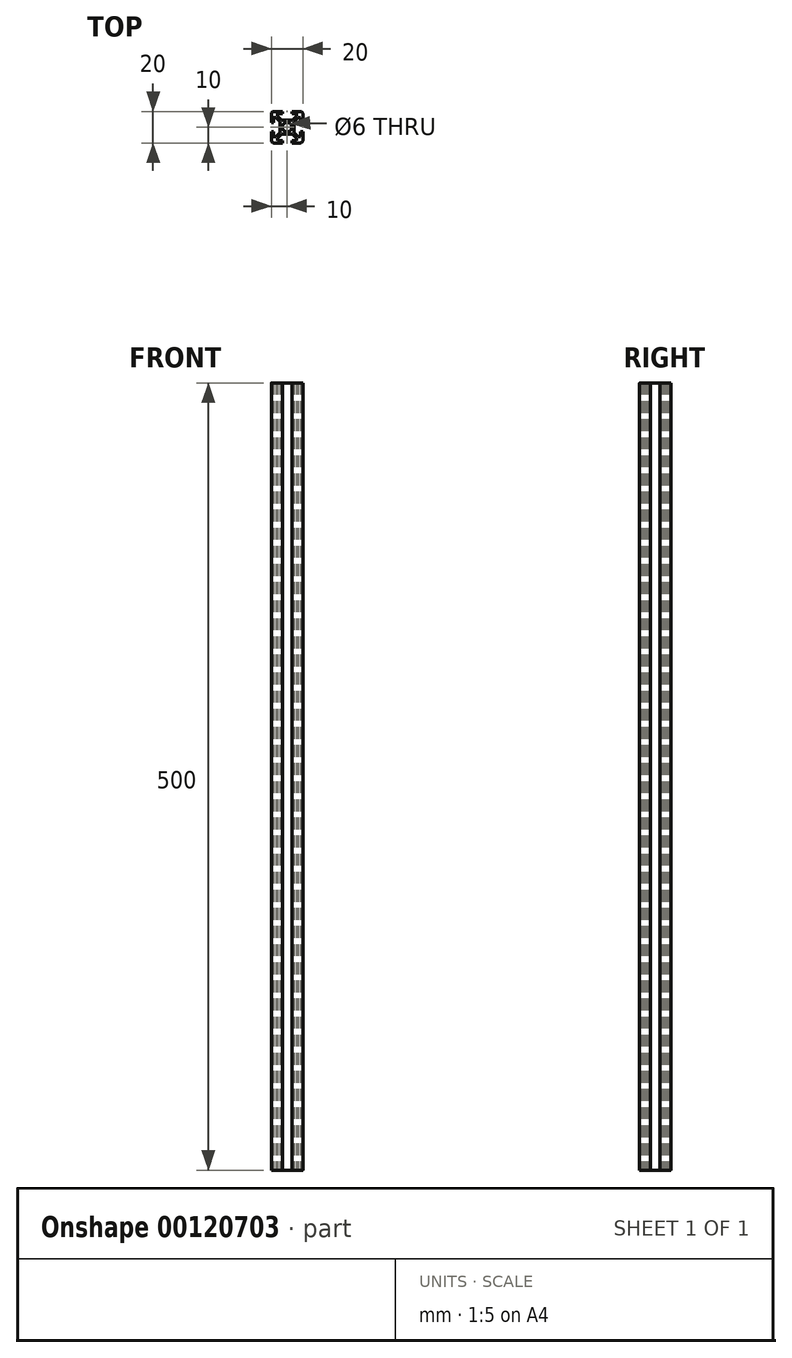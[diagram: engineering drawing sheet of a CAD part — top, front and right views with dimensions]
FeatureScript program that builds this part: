
annotation { "Feature Type Name" : "Feature", "Feature Type Description" : "" }
export const myFeature = defineFeature(function(context is Context, id is Id, definition is map)
    precondition{}
    {
        {
            var Q0;
            Q0=qCreatedBy(makeId("Top.planeOp"),FACE);
            var sketch = newSketch(context, id + "F0", { "sketchPlane" : qUnion([Q0])});
            skLineSegment(sketch, "E0.bottom", {"start": v(1.5, 0) * mm, "end": v(7, 0) * mm});
            skLineSegment(sketch, "E0.top", {"start": v(1.5, 20) * mm, "end": v(7, 20) * mm});
            skLineSegment(sketch, "E0.left", {"start": v(0, 1.5) * mm, "end": v(0, 7) * mm});
            skLineSegment(sketch, "E0.right", {"start": v(20, 1.5) * mm, "end": v(20, 7) * mm});
            skLineSegment(sketch, "E1", {"start": v(10, 25.59) * mm, "end": v(10, -6.26) * mm, "construction": true});
            skPoint(sketch, "E1.startSnap0", {"position": v(10, 20) * mm});
            skLineSegment(sketch, "E2", {"start": v(-5.38, 10) * mm, "end": v(26.16, 10) * mm, "construction": true});
            skPoint(sketch, "E2.startSnap0", {"position": v(0, 10) * mm});
            skPoint(sketch, "E3.visualSharp", {"position": v(20, 20) * mm});
            skArc(sketch, "E3.filletArc", {"start": v(20, 18.5) * mm, "mid": v(19.56, 19.56) * mm, "end": v(18.5, 20) * mm});
            skPoint(sketch, "E4.visualSharp", {"position": v(20, 0) * mm});
            skArc(sketch, "E4.filletArc", {"start": v(18.5, 0) * mm, "mid": v(19.56, 0.44) * mm, "end": v(20, 1.5) * mm});
            skPoint(sketch, "E5.visualSharp", {"position": v(0, 0) * mm});
            skArc(sketch, "E5.filletArc", {"start": v(0, 1.5) * mm, "mid": v(0.44, 0.44) * mm, "end": v(1.5, 0) * mm});
            skPoint(sketch, "E6.visualSharp", {"position": v(0, 20) * mm});
            skArc(sketch, "E6.filletArc", {"start": v(1.5, 20) * mm, "mid": v(0.44, 19.56) * mm, "end": v(0, 18.5) * mm});
            skLineSegment(sketch, "E7", {"start": v(20, 13) * mm, "end": v(18.5, 13) * mm});
            skLineSegment(sketch, "E8", {"start": v(18.5, 13) * mm, "end": v(18.5, 16) * mm});
            skLineSegment(sketch, "E9", {"start": v(18.5, 16) * mm, "end": v(17, 16) * mm});
            skLineSegment(sketch, "E10", {"start": v(17, 16) * mm, "end": v(14.5, 13.5) * mm});
            skLineSegment(sketch, "E11", {"start": v(14.5, 13.5) * mm, "end": v(14.5, 10) * mm});
            skLineSegment(sketch, "E12.MirrorCS", {"start": v(20, 7) * mm, "end": v(18.5, 7) * mm});
            skLineSegment(sketch, "E13.MirrorCS", {"start": v(18.5, 7) * mm, "end": v(18.5, 4) * mm});
            skLineSegment(sketch, "E14.MirrorCS", {"start": v(18.5, 4) * mm, "end": v(17, 4) * mm});
            skLineSegment(sketch, "E15.MirrorCS", {"start": v(14.5, 6.5) * mm, "end": v(14.5, 10) * mm});
            skLineSegment(sketch, "E16.MirrorCS", {"start": v(17, 4) * mm, "end": v(14.5, 6.5) * mm});
            skLineSegment(sketch, "E17.MirrorCS", {"start": v(0, 13) * mm, "end": v(1.5, 13) * mm});
            skLineSegment(sketch, "E18.MirrorCS", {"start": v(1.5, 13) * mm, "end": v(1.5, 16) * mm});
            skLineSegment(sketch, "E19.MirrorCS", {"start": v(1.5, 16) * mm, "end": v(3, 16) * mm});
            skLineSegment(sketch, "E20.MirrorCS", {"start": v(3, 16) * mm, "end": v(5.5, 13.5) * mm});
            skLineSegment(sketch, "E21.MirrorCS", {"start": v(5.5, 13.5) * mm, "end": v(5.5, 10) * mm});
            skLineSegment(sketch, "E22.MirrorCS", {"start": v(5.5, 6.5) * mm, "end": v(5.5, 10) * mm});
            skLineSegment(sketch, "E23.MirrorCS", {"start": v(3, 4) * mm, "end": v(5.5, 6.5) * mm});
            skLineSegment(sketch, "E24.MirrorCS", {"start": v(1.5, 4) * mm, "end": v(3, 4) * mm});
            skLineSegment(sketch, "E25.MirrorCS", {"start": v(1.5, 7) * mm, "end": v(1.5, 4) * mm});
            skLineSegment(sketch, "E26.MirrorCS", {"start": v(0, 7) * mm, "end": v(1.5, 7) * mm});
            skLineSegment(sketch, "E27.1.0", {"start": v(13, 20) * mm, "end": v(13, 18.5) * mm});
            skLineSegment(sketch, "E27.1.1", {"start": v(13, 18.5) * mm, "end": v(16, 18.5) * mm});
            skLineSegment(sketch, "E27.1.2", {"start": v(16, 18.5) * mm, "end": v(16, 17) * mm});
            skLineSegment(sketch, "E27.1.3", {"start": v(16, 17) * mm, "end": v(13.5, 14.5) * mm});
            skLineSegment(sketch, "E27.1.4", {"start": v(13.5, 14.5) * mm, "end": v(10, 14.5) * mm});
            skLineSegment(sketch, "E27.1.5", {"start": v(6.5, 14.5) * mm, "end": v(10, 14.5) * mm});
            skLineSegment(sketch, "E27.1.6", {"start": v(4, 17) * mm, "end": v(6.5, 14.5) * mm});
            skLineSegment(sketch, "E27.1.7", {"start": v(4, 18.5) * mm, "end": v(4, 17) * mm});
            skLineSegment(sketch, "E27.1.8", {"start": v(7, 18.5) * mm, "end": v(4, 18.5) * mm});
            skLineSegment(sketch, "E27.1.9", {"start": v(7, 20) * mm, "end": v(7, 18.5) * mm});
            skPoint(sketch, "E27.center", {"position": v(10, 10) * mm});
            skLineSegment(sketch, "E27.anchor1", {"start": v(10, 10) * mm, "end": v(0, 13) * mm, "construction": true});
            skLineSegment(sketch, "E27.anchor2", {"start": v(10, 10) * mm, "end": v(13, 20) * mm, "construction": true});
            skLineSegment(sketch, "E28.MirrorCS", {"start": v(7, 0) * mm, "end": v(7, 1.5) * mm});
            skLineSegment(sketch, "E29.MirrorCS", {"start": v(7, 1.5) * mm, "end": v(4, 1.5) * mm});
            skLineSegment(sketch, "E30.MirrorCS", {"start": v(4, 1.5) * mm, "end": v(4, 3) * mm});
            skLineSegment(sketch, "E31.MirrorCS", {"start": v(4, 3) * mm, "end": v(6.5, 5.5) * mm});
            skLineSegment(sketch, "E32.MirrorCS", {"start": v(6.5, 5.5) * mm, "end": v(10, 5.5) * mm});
            skLineSegment(sketch, "E33.MirrorCS", {"start": v(13.5, 5.5) * mm, "end": v(10, 5.5) * mm});
            skLineSegment(sketch, "E34.MirrorCS", {"start": v(16, 3) * mm, "end": v(13.5, 5.5) * mm});
            skLineSegment(sketch, "E35.MirrorCS", {"start": v(16, 1.5) * mm, "end": v(16, 3) * mm});
            skLineSegment(sketch, "E36.MirrorCS", {"start": v(13, 1.5) * mm, "end": v(16, 1.5) * mm});
            skLineSegment(sketch, "E37.MirrorCS", {"start": v(13, 0) * mm, "end": v(13, 1.5) * mm});
            skLineSegment(sketch, "E38.trimOffspring", {"start": v(13, 20) * mm, "end": v(18.5, 20) * mm});
            skLineSegment(sketch, "E39.trimOffspring", {"start": v(20, 13) * mm, "end": v(20, 18.5) * mm});
            skLineSegment(sketch, "E40.trimOffspring", {"start": v(13, 0) * mm, "end": v(18.5, 0) * mm});
            skLineSegment(sketch, "E41.trimOffspring", {"start": v(0, 13) * mm, "end": v(0, 18.5) * mm});
            skCircle(sketch, "E42", {"center": v(10, 10) * mm, "radius": 3 * mm});
            skSolve(sketch);
        }
        {
            var Q0;
            Q0=qSketchRegion(id+"F0",true);
            extrude(context, id + "F1", {"entities" : qUnion([Q0]), "depth" : 500 * mm});
        }
    });
